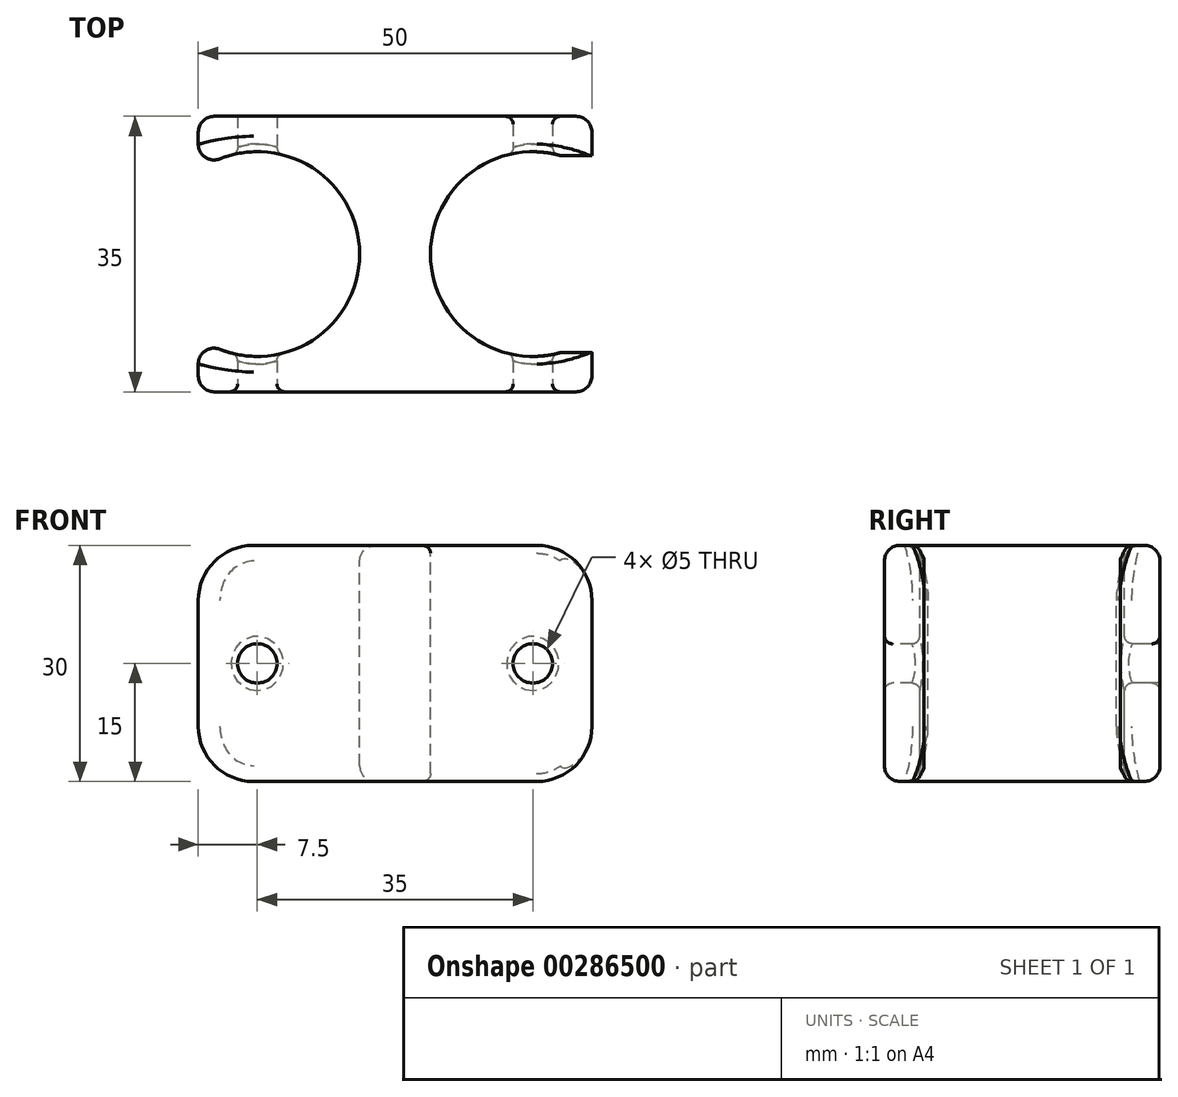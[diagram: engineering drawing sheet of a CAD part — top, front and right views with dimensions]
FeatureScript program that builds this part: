
annotation { "Feature Type Name" : "Feature", "Feature Type Description" : "" }
export const myFeature = defineFeature(function(context is Context, id is Id, definition is map)
    precondition{}
    {
        {
            var Q0;
            Q0=qCreatedBy(makeId("Top.planeOp"),FACE);
            var sketch = newSketch(context, id + "F0", { "sketchPlane" : qUnion([Q0])});
            skLineSegment(sketch, "E0.bottom", {"start": v(25, 17.5) * mm, "end": v(-25, 17.5) * mm});
            skLineSegment(sketch, "E0.top", {"start": v(25, -17.5) * mm, "end": v(-25, -17.5) * mm});
            skLineSegment(sketch, "E0.left", {"start": v(25, 17.5) * mm, "end": v(25, -17.5) * mm});
            skLineSegment(sketch, "E0.right", {"start": v(-25, 17.5) * mm, "end": v(-25, -17.5) * mm});
            skPoint(sketch, "E0.middle", {"position": v(0, 0) * mm});
            skSolve(sketch);
        }
        {
            var Q0;
            Q0 = qSketchRegion(id + "F0", true);
            extrude(context, id + "F1", {"entities" : qUnion([Q0]), "depth" : 30 * mm, "offsetDistance" : 25 * mm, "symmetric" : true});
        }
        {
            var Q0;
            Q0=qCreatedBy(makeId("Top.planeOp"),FACE);
            var sketch = newSketch(context, id + "F2", { "sketchPlane" : qUnion([Q0])});
            skCircle(sketch, "E1", {"center": v(-17.5, 0) * mm, "radius": 13 * mm});
            skCircle(sketch, "E2.MirrorC", {"center": v(17.5, 0) * mm, "radius": 13 * mm});
            skLineSegment(sketch, "E3", {"start": v(17.5, 13) * mm, "end": v(17.5, -13) * mm});
            skLineSegment(sketch, "E4.bottom", {"start": v(21.07, 12.5) * mm, "end": v(41.07, 12.5) * mm});
            skLineSegment(sketch, "E4.top", {"start": v(21.07, -12.5) * mm, "end": v(41.07, -12.5) * mm});
            skLineSegment(sketch, "E4.left", {"start": v(21.07, 12.5) * mm, "end": v(21.07, -12.5) * mm});
            skLineSegment(sketch, "E4.right", {"start": v(41.07, 12.5) * mm, "end": v(41.07, -12.5) * mm});
            skPoint(sketch, "E4.middle", {"position": v(31.07, 0) * mm});
            skSolve(sketch);
        }
        {
            var Q0;
            Q0 = qSketchRegion(id + "F2", true);
            extrude(context, id + "F3", {"entities" : qUnion([Q0]), "operationType" : NewBodyOperationType.REMOVE, "endBound" : BoundingType.THROUGH_ALL, "oppositeDirection" : true, "depth" : 25 * mm, "offsetDistance" : 25 * mm, "hasSecondDirection" : true, "secondDirectionBound" : BoundingType.THROUGH_ALL, "secondDirectionOppositeDirection" : false, "secondDirectionDepth" : 25 * mm});
        }
        {
            var Q0;
            {var subQ0=sQuery(id+"F0.wireOp",EDGE,"E0.right");var subQ1=sQuery(id+"F0.wireOp",EDGE,"E0.top");Q0=makeQuery(id+"F3.boolean.opBoolean","SPLIT",EDGE,{"disambiguationData":[TD([makeQuery(id+"F1.opExtrude","SWEPT_FACE",FACE,{"disambiguationData":[OSD([subQ1])]})])],"derivedFrom":makeQuery(id+"F1.opExtrude","CAP_EDGE",EDGE,{"disambiguationData":[OSD([subQ0])],"isStart":false})});}
            var Q1;
            {var subQ0=sQuery(id+"F0.wireOp",EDGE,"E0.left");var subQ1=sQuery(id+"F0.wireOp",EDGE,"E0.top");Q1=makeQuery(id+"F3.boolean.opBoolean","SPLIT",EDGE,{"disambiguationData":[TD([makeQuery(id+"F1.opExtrude","SWEPT_FACE",FACE,{"disambiguationData":[OSD([subQ1])]})])],"derivedFrom":makeQuery(id+"F1.opExtrude","CAP_EDGE",EDGE,{"disambiguationData":[OSD([subQ0])],"isStart":false})});}
            var Q2;
            {var subQ0=sQuery(id+"F0.wireOp",EDGE,"E0.bottom");var subQ1=sQuery(id+"F0.wireOp",EDGE,"E0.right");Q2=makeQuery(id+"F3.boolean.opBoolean","SPLIT",EDGE,{"disambiguationData":[TD([makeQuery(id+"F1.opExtrude","SWEPT_FACE",FACE,{"disambiguationData":[OSD([subQ0])]})])],"derivedFrom":makeQuery(id+"F1.opExtrude","CAP_EDGE",EDGE,{"disambiguationData":[OSD([subQ1])],"isStart":false})});}
            var Q3;
            {var subQ0=sQuery(id+"F0.wireOp",EDGE,"E0.bottom");var subQ1=sQuery(id+"F0.wireOp",EDGE,"E0.left");Q3=makeQuery(id+"F3.boolean.opBoolean","SPLIT",EDGE,{"disambiguationData":[TD([makeQuery(id+"F1.opExtrude","SWEPT_FACE",FACE,{"disambiguationData":[OSD([subQ0])]})])],"derivedFrom":makeQuery(id+"F1.opExtrude","CAP_EDGE",EDGE,{"disambiguationData":[OSD([subQ1])],"isStart":false})});}
            var Q4;
            {var subQ0=sQuery(id+"F0.wireOp",EDGE,"E0.left");var subQ1=sQuery(id+"F0.wireOp",EDGE,"E0.top");Q4=makeQuery(id+"F3.boolean.opBoolean","SPLIT",EDGE,{"disambiguationData":[TD([makeQuery(id+"F1.opExtrude","SWEPT_FACE",FACE,{"disambiguationData":[OSD([subQ1])]})])],"derivedFrom":makeQuery(id+"F1.opExtrude","CAP_EDGE",EDGE,{"disambiguationData":[OSD([subQ0])],"isStart":true})});}
            var Q5;
            {var subQ0=sQuery(id+"F0.wireOp",EDGE,"E0.bottom");var subQ1=sQuery(id+"F0.wireOp",EDGE,"E0.left");Q5=makeQuery(id+"F3.boolean.opBoolean","SPLIT",EDGE,{"disambiguationData":[TD([makeQuery(id+"F1.opExtrude","SWEPT_FACE",FACE,{"disambiguationData":[OSD([subQ0])]})])],"derivedFrom":makeQuery(id+"F1.opExtrude","CAP_EDGE",EDGE,{"disambiguationData":[OSD([subQ1])],"isStart":true})});}
            var Q6;
            {var subQ0=sQuery(id+"F0.wireOp",EDGE,"E0.right");var subQ1=sQuery(id+"F0.wireOp",EDGE,"E0.top");Q6=makeQuery(id+"F3.boolean.opBoolean","SPLIT",EDGE,{"disambiguationData":[TD([makeQuery(id+"F1.opExtrude","SWEPT_FACE",FACE,{"disambiguationData":[OSD([subQ1])]})])],"derivedFrom":makeQuery(id+"F1.opExtrude","CAP_EDGE",EDGE,{"disambiguationData":[OSD([subQ0])],"isStart":true})});}
            var Q7;
            {var subQ0=sQuery(id+"F0.wireOp",EDGE,"E0.bottom");var subQ1=sQuery(id+"F0.wireOp",EDGE,"E0.right");Q7=makeQuery(id+"F3.boolean.opBoolean","SPLIT",EDGE,{"disambiguationData":[TD([makeQuery(id+"F1.opExtrude","SWEPT_FACE",FACE,{"disambiguationData":[OSD([subQ0])]})])],"derivedFrom":makeQuery(id+"F1.opExtrude","CAP_EDGE",EDGE,{"disambiguationData":[OSD([subQ1])],"isStart":true})});}
            fillet(context, id + "F4", {"entities" : qUnion([Q0, Q1, Q2, Q3, Q4, Q5, Q6, Q7]), "radius" : 7 * mm, "tangentPropagation" : true, "allowEdgeOverflow" : false});
        }
        {
            var Q0;
            Q0=makeQuery(id+"F1.opExtrude","CAP_EDGE",EDGE,{"disambiguationData":[OSD([sQuery(id+"F0.wireOp",EDGE,"E0.top")])],"isStart":false});
            var Q1;
            Q1=makeQuery(id+"F1.opExtrude","CAP_EDGE",EDGE,{"disambiguationData":[OSD([sQuery(id+"F0.wireOp",EDGE,"E0.bottom")])],"isStart":false});
            var Q2;
            Q2=makeQuery(id+"F1.opExtrude","CAP_EDGE",EDGE,{"disambiguationData":[OSD([sQuery(id+"F0.wireOp",EDGE,"E0.top")])],"isStart":true});
            var Q3;
            Q3=makeQuery(id+"F1.opExtrude","CAP_EDGE",EDGE,{"disambiguationData":[OSD([sQuery(id+"F0.wireOp",EDGE,"E0.bottom")])],"isStart":true});
            var Q4;
            Q4=makeQuery(id+"F1.opExtrude","SWEPT_EDGE",EDGE,{"disambiguationData":[OSD([sQuery(id+"F0.wireOp",EDGE,"E0.top"),sQuery(id+"F0.wireOp",EDGE,"E0.left")])]});
            var Q5;
            Q5=makeQuery(id+"F1.opExtrude","SWEPT_EDGE",EDGE,{"disambiguationData":[OSD([sQuery(id+"F0.wireOp",EDGE,"E0.bottom"),sQuery(id+"F0.wireOp",EDGE,"E0.left")])]});
            var Q6;
            Q6=makeQuery(id+"F1.opExtrude","SWEPT_EDGE",EDGE,{"disambiguationData":[OSD([sQuery(id+"F0.wireOp",EDGE,"E0.top"),sQuery(id+"F0.wireOp",EDGE,"E0.right")])]});
            var Q7;
            Q7=makeQuery(id+"F1.opExtrude","SWEPT_EDGE",EDGE,{"disambiguationData":[OSD([sQuery(id+"F0.wireOp",EDGE,"E0.bottom"),sQuery(id+"F0.wireOp",EDGE,"E0.right")])]});
            var Q8;
            Q8=makeQuery(id+"F3.boolean.opBoolean","COPY",EDGE,{"derivedFrom":makeQuery(id+"F3.opExtrude","CAP_EDGE",EDGE,{"disambiguationData":[OSD([sQuery(id+"F2.wireOp",EDGE,"E1")])],"isStart":true})});
            var Q9;
            Q9=makeQuery(id+"F3.boolean.opBoolean","COPY",EDGE,{"derivedFrom":makeQuery(id+"F3.opExtrude","CAP_EDGE",EDGE,{"disambiguationData":[OSD([sQuery(id+"F2.wireOp",EDGE,"E2.MirrorC")])],"isStart":true})});
            var Q10;
            Q10=makeQuery(id+"F3.boolean.opBoolean","INTERSECT",EDGE,{"derivedFrom":[makeQuery(id+"F1.opExtrude","CAP_FACE",FACE,{"disambiguationData":[OSD([sQuery(id+"F0.wireOp",EDGE,"E0.bottom"),sQuery(id+"F0.wireOp",EDGE,"E0.top"),sQuery(id+"F0.wireOp",EDGE,"E0.left"),sQuery(id+"F0.wireOp",EDGE,"E0.right")])],"isStart":true}),makeQuery(id+"F3.opExtrude","SWEPT_FACE",FACE,{"disambiguationData":[OSD([sQuery(id+"F2.wireOp",EDGE,"E1")])]})]});
            fillet(context, id + "F5", {"entities" : qUnion([Q0, Q1, Q2, Q3, Q4, Q5, Q6, Q7, Q8, Q9, Q10]), "radius" : 2 * mm, "tangentPropagation" : true, "allowEdgeOverflow" : false});
        }
        {
            var Q0;
            Q0=makeQuery(id+"F3.boolean.opBoolean","INTERSECT",EDGE,{"derivedFrom":[makeQuery(id+"F1.opExtrude","CAP_FACE",FACE,{"disambiguationData":[OSD([sQuery(id+"F0.wireOp",EDGE,"E0.bottom"),sQuery(id+"F0.wireOp",EDGE,"E0.top"),sQuery(id+"F0.wireOp",EDGE,"E0.left"),sQuery(id+"F0.wireOp",EDGE,"E0.right")])],"isStart":false}),makeQuery(id+"F3.opExtrude","SWEPT_FACE",FACE,{"disambiguationData":[OSD([sQuery(id+"F2.wireOp",EDGE,"E2.MirrorC")])]})]});
            var Q1;
            Q1=makeQuery(id+"F3.boolean.opBoolean","INTERSECT",EDGE,{"derivedFrom":[makeQuery(id+"F1.opExtrude","CAP_FACE",FACE,{"disambiguationData":[OSD([sQuery(id+"F0.wireOp",EDGE,"E0.bottom"),sQuery(id+"F0.wireOp",EDGE,"E0.top"),sQuery(id+"F0.wireOp",EDGE,"E0.left"),sQuery(id+"F0.wireOp",EDGE,"E0.right")])],"isStart":true}),makeQuery(id+"F3.opExtrude","SWEPT_FACE",FACE,{"disambiguationData":[OSD([sQuery(id+"F2.wireOp",EDGE,"E2.MirrorC")])]})]});
            var Q2;
            Q2=makeQuery(id+"F3.boolean.opBoolean","COPY",FACE,{"derivedFrom":makeQuery(id+"F3.opExtrude","SWEPT_FACE",FACE,{"disambiguationData":[OSD([sQuery(id+"F2.wireOp",EDGE,"E2.MirrorC")])]})});
            fillet(context, id + "F6", {"entities" : qUnion([Q0, Q1, Q2]), "radius" : 1 * mm, "tangentPropagation" : true, "allowEdgeOverflow" : false});
        }
        {
            var Q0;
            Q0=qCreatedBy(makeId("Front.planeOp"),FACE);
            var sketch = newSketch(context, id + "F7", { "sketchPlane" : qUnion([Q0])});
            skPoint(sketch, "E5.0", {"position": v(-17.5, 0) * mm});
            skPoint(sketch, "E6.0", {"position": v(17.5, 0) * mm});
            skCircle(sketch, "E7", {"center": v(-17.5, 0) * mm, "radius": 2.5 * mm});
            skCircle(sketch, "E8", {"center": v(17.5, 0) * mm, "radius": 2.5 * mm});
            skSolve(sketch);
        }
        {
            var Q0;
            Q0 = qSketchRegion(id + "F7", true);
            extrude(context, id + "F8", {"entities" : qUnion([Q0]), "operationType" : NewBodyOperationType.REMOVE, "endBound" : BoundingType.THROUGH_ALL, "oppositeDirection" : true, "depth" : 25 * mm, "offsetDistance" : 25 * mm, "hasSecondDirection" : true, "secondDirectionBound" : BoundingType.THROUGH_ALL, "secondDirectionOppositeDirection" : false, "secondDirectionDepth" : 25 * mm});
        }
        {
            var Q0;
            Q0=makeQuery(id+"F8.boolean.opBoolean","COPY",FACE,{"disambiguationData":[TD([makeQuery(id+"F1.opExtrude","SWEPT_FACE",FACE,{"disambiguationData":[OSD([sQuery(id+"F0.wireOp",EDGE,"E0.top")])]})])],"derivedFrom":makeQuery(id+"F8.opExtrude","SWEPT_FACE",FACE,{"disambiguationData":[OSD([sQuery(id+"F7.wireOp",EDGE,"E7")])]})});
            var Q1;
            Q1=makeQuery(id+"F8.boolean.opBoolean","COPY",FACE,{"disambiguationData":[TD([makeQuery(id+"F1.opExtrude","SWEPT_FACE",FACE,{"disambiguationData":[OSD([sQuery(id+"F0.wireOp",EDGE,"E0.top")])]})])],"derivedFrom":makeQuery(id+"F8.opExtrude","SWEPT_FACE",FACE,{"disambiguationData":[OSD([sQuery(id+"F7.wireOp",EDGE,"E8")])]})});
            var Q2;
            Q2=makeQuery(id+"F8.boolean.opBoolean","INTERSECT",EDGE,{"disambiguationData":[OD(0.0)],"derivedFrom":[makeQuery(id+"F3.boolean.opBoolean","COPY",FACE,{"derivedFrom":makeQuery(id+"F3.opExtrude","SWEPT_FACE",FACE,{"disambiguationData":[OSD([sQuery(id+"F2.wireOp",EDGE,"E1")])]})}),makeQuery(id+"F8.opExtrude","SWEPT_FACE",FACE,{"disambiguationData":[OSD([sQuery(id+"F7.wireOp",EDGE,"E7")])]})]});
            var Q3;
            Q3=makeQuery(id+"F8.boolean.opBoolean","COPY",FACE,{"disambiguationData":[TD([makeQuery(id+"F1.opExtrude","SWEPT_FACE",FACE,{"disambiguationData":[OSD([sQuery(id+"F0.wireOp",EDGE,"E0.bottom")])]})])],"derivedFrom":makeQuery(id+"F8.opExtrude","SWEPT_FACE",FACE,{"disambiguationData":[OSD([sQuery(id+"F7.wireOp",EDGE,"E8")])]})});
            fillet(context, id + "F9", {"entities" : qUnion([Q0, Q1, Q2, Q3]), "radius" : 1 * mm, "tangentPropagation" : true, "allowEdgeOverflow" : false});
        }
    });
